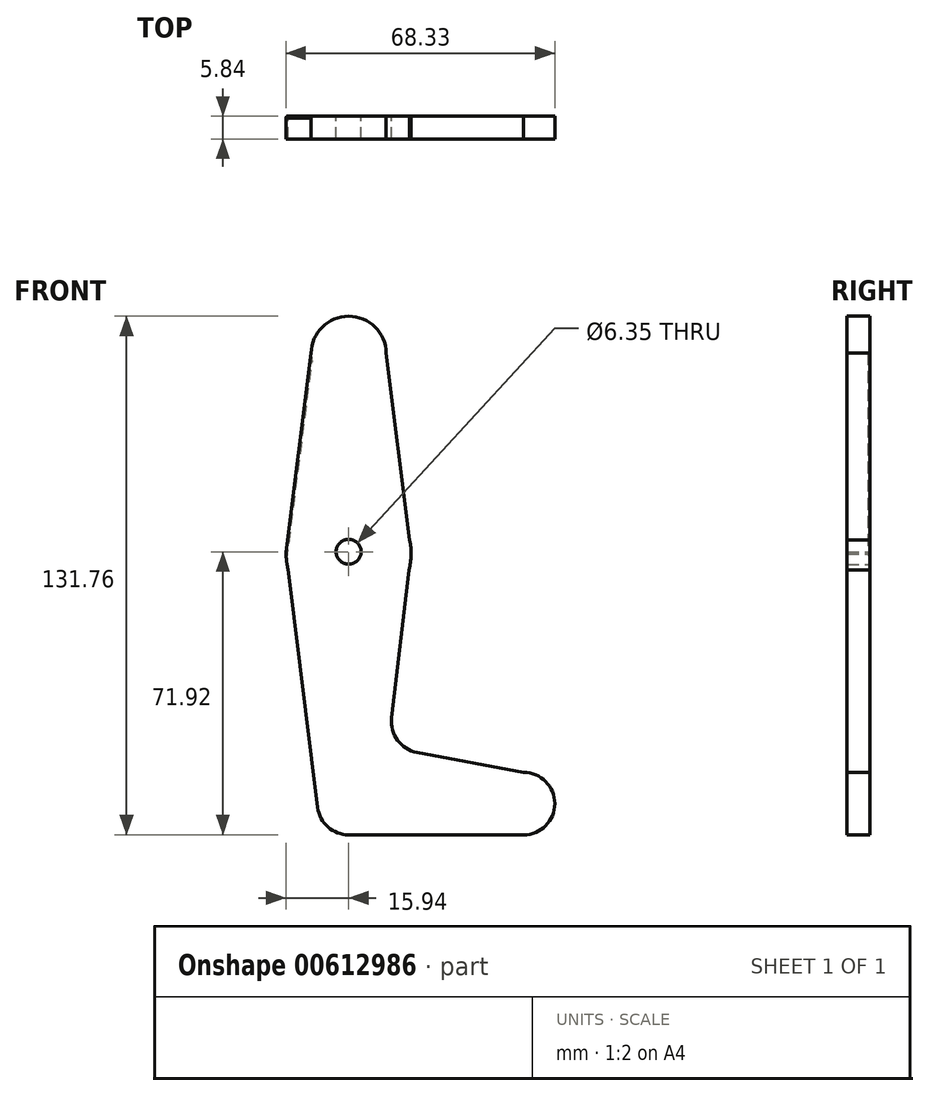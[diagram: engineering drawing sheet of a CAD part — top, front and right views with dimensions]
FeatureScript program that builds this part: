
annotation { "Feature Type Name" : "Feature", "Feature Type Description" : "" }
export const myFeature = defineFeature(function(context is Context, id is Id, definition is map)
    precondition{}
    {
        {
            var Q0;
            Q0=qCreatedBy(makeId("Front.planeOp"),FACE);
            var sketch = newSketch(context, id + "F0", { "sketchPlane" : qUnion([Q0])});
            skCircle(sketch, "E0", {"center": v(0, 50.31) * mm, "radius": 9.53 * mm});
            skCircle(sketch, "E1", {"center": v(0, -0.49) * mm, "radius": 15.88 * mm});
            skCircle(sketch, "E2", {"center": v(0, -63.99) * mm, "radius": 7.94 * mm});
            skCircle(sketch, "E3", {"center": v(44.45, -63.99) * mm, "radius": 7.94 * mm});
            skLineSegment(sketch, "E4", {"start": v(0, 50.31) * mm, "end": v(0, -63.99) * mm, "construction": true});
            skLineSegment(sketch, "E5", {"start": v(0, -63.99) * mm, "end": v(44.45, -63.99) * mm, "construction": true});
            skLineSegment(sketch, "E6", {"start": v(-9.52, 50.46) * mm, "end": v(-15.94, 0) * mm});
            skLineSegment(sketch, "E7", {"start": v(-15.94, 0) * mm, "end": v(-7.88, -64.96) * mm});
            skLineSegment(sketch, "E8", {"start": v(9.52, 50.44) * mm, "end": v(15.87, 0) * mm});
            skLineSegment(sketch, "E9", {"start": v(0, -71.92) * mm, "end": v(44.45, -71.92) * mm});
            skArc(sketch, "E10", {"start": v(10.95, -42.29) * mm, "mid": v(12.45, -47.91) * mm, "end": v(17.38, -51) * mm});
            skLineSegment(sketch, "E11", {"start": v(15.87, 0) * mm, "end": v(10.95, -42.29) * mm});
            skLineSegment(sketch, "E12", {"start": v(44.45, -56.05) * mm, "end": v(17.38, -51) * mm});
            skSolve(sketch);
        }
        {
            var Q0;
            Q0 = qSketchRegion(id + "F0", true);
            extrude(context, id + "F1", {"entities" : qUnion([Q0]), "depth" : 5.84 * mm, "offsetDistance" : 25.4 * mm});
        }
        {
            var Q0;
            Q0=makeQuery(id+"F1.opExtrude","CAP_FACE",FACE,{"disambiguationData":[OSD([sQuery(id+"F0.wireOp",EDGE,"E0"),sQuery(id+"F0.wireOp",EDGE,"E1"),sQuery(id+"F0.wireOp",EDGE,"E2"),sQuery(id+"F0.wireOp",EDGE,"E3"),sQuery(id+"F0.wireOp",EDGE,"E6"),sQuery(id+"F0.wireOp",EDGE,"E7"),sQuery(id+"F0.wireOp",EDGE,"E8"),sQuery(id+"F0.wireOp",EDGE,"E9"),sQuery(id+"F0.wireOp",EDGE,"E10"),sQuery(id+"F0.wireOp",EDGE,"E11"),sQuery(id+"F0.wireOp",EDGE,"E12")])],"isStart":true});
            var sketch = newSketch(context, id + "F2", { "sketchPlane" : qUnion([Q0])});
            skPoint(sketch, "E13", {"position": v(0, 0) * mm});
            skSolve(sketch);
        }
        {
            var Q0;
            Q0=sQuery(id+"F2.wireOp",VERTEX,"E13");
            var Q1;
            Q1=makeQuery(id+"F1.opExtrude","SWEPT_BODY",BODY,{"disambiguationData":[OSD([sQuery(id+"F0.wireOp",EDGE,"E0"),sQuery(id+"F0.wireOp",EDGE,"E1"),sQuery(id+"F0.wireOp",EDGE,"E2"),sQuery(id+"F0.wireOp",EDGE,"E3"),sQuery(id+"F0.wireOp",EDGE,"E6"),sQuery(id+"F0.wireOp",EDGE,"E7"),sQuery(id+"F0.wireOp",EDGE,"E8"),sQuery(id+"F0.wireOp",EDGE,"E9"),sQuery(id+"F0.wireOp",EDGE,"E10"),sQuery(id+"F0.wireOp",EDGE,"E11"),sQuery(id+"F0.wireOp",EDGE,"E12")])]});
            hole(context, id + "F3", {"style" : HoleStyle.SIMPLE, "endStyle" : HoleEndStyle.THROUGH, "holeDiameter" : 6.35 * mm, "majorDiameter" : 6.35 * mm, "isTappedThrough" : true, "tappedDepth" : 12.7 * mm, "tapClearance" : 3, "locations" : qUnion([Q0]), "scope" : qUnion([Q1])});
        }
        {
            var Q0;
            Q0=makeQuery(id+"F1.opExtrude","CAP_EDGE",EDGE,{"disambiguationData":[OSD([sQuery(id+"F0.wireOp",EDGE,"E6")])],"isStart":true});
            chamfer(context, id + "F4", {"entities" : qUnion([Q0]), "width" : 0.5 * mm, "tangentPropagation" : true});
        }
    });
